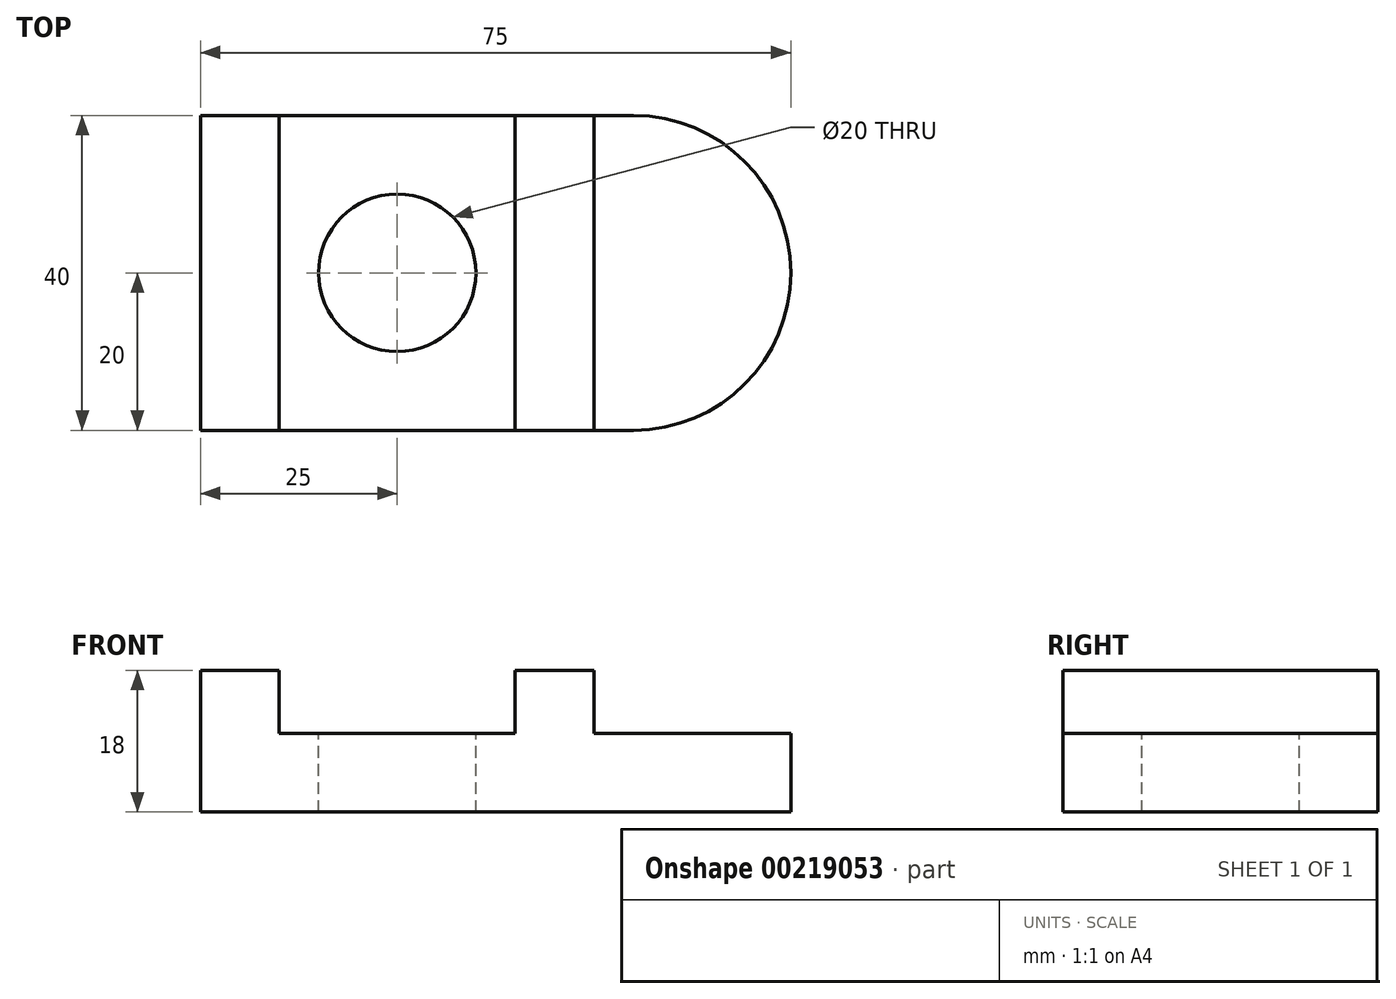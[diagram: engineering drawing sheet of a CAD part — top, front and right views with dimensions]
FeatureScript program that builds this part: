
annotation { "Feature Type Name" : "Feature", "Feature Type Description" : "" }
export const myFeature = defineFeature(function(context is Context, id is Id, definition is map)
    precondition{}
    {
        {
            var Q0;
            Q0=qCreatedBy(makeId("Front.planeOp"),FACE);
            var sketch = newSketch(context, id + "F0", { "sketchPlane" : qUnion([Q0])});
            skLineSegment(sketch, "E0", {"start": v(0, 0) * mm, "end": v(75, 0) * mm});
            skLineSegment(sketch, "E1", {"start": v(75, 0) * mm, "end": v(75, 10) * mm});
            skLineSegment(sketch, "E2", {"start": v(75, 10) * mm, "end": v(50, 10) * mm});
            skLineSegment(sketch, "E3", {"start": v(50, 10) * mm, "end": v(50, 18) * mm});
            skLineSegment(sketch, "E4", {"start": v(50, 18) * mm, "end": v(40, 18) * mm});
            skLineSegment(sketch, "E5", {"start": v(40, 18) * mm, "end": v(40, 10) * mm});
            skLineSegment(sketch, "E6", {"start": v(40, 10) * mm, "end": v(10, 10) * mm});
            skLineSegment(sketch, "E7", {"start": v(10, 10) * mm, "end": v(10, 18) * mm});
            skLineSegment(sketch, "E8", {"start": v(10, 18) * mm, "end": v(0, 18) * mm});
            skLineSegment(sketch, "E9", {"start": v(0, 18) * mm, "end": v(0, 0) * mm});
            skSolve(sketch);
        }
        {
            var Q0;
            Q0 = qSketchRegion(id + "F0", true);
            extrude(context, id + "F1", {"entities" : qUnion([Q0]), "depth" : 40 * mm});
        }
        {
            var Q0;
            Q0=makeQuery(id+"F1.opExtrude","CAP_EDGE",EDGE,{"disambiguationData":[OSD([sQuery(id+"F0.wireOp",EDGE,"E1")])],"isStart":false});
            var Q1;
            Q1=makeQuery(id+"F1.opExtrude","CAP_EDGE",EDGE,{"disambiguationData":[OSD([sQuery(id+"F0.wireOp",EDGE,"E1")])],"isStart":true});
            fillet(context, id + "F2", {"entities" : qUnion([Q0, Q1]), "radius" : 20 * mm, "tangentPropagation" : true, "allowEdgeOverflow" : false});
        }
        {
            var Q0;
            Q0=makeQuery(id+"F1.opExtrude","SWEPT_FACE",FACE,{"disambiguationData":[OSD([sQuery(id+"F0.wireOp",EDGE,"E6")])]});
            var sketch = newSketch(context, id + "F3", { "sketchPlane" : qUnion([Q0])});
            skCircle(sketch, "E10", {"center": v(25, -20) * mm, "radius": 10 * mm});
            skPoint(sketch, "E10.centerSnap0", {"position": v(40, -20) * mm});
            skPoint(sketch, "E10.centerSnap1", {"position": v(25, 0) * mm});
            skSolve(sketch);
        }
        {
            var Q0;
            Q0=makeQuery(id+"F3.imprint","IMPRINT",FACE,{"disambiguationData":[TD([[makeQuery(id+"F3.imprint","IMPRINT",EDGE,{"derivedFrom":sQuery(id+"F3.wireOp",EDGE,"E10")}),1.0]])]});
            extrude(context, id + "F4", {"entities" : qUnion([Q0]), "operationType" : NewBodyOperationType.REMOVE, "endBound" : BoundingType.UP_TO_NEXT, "oppositeDirection" : true, "depth" : 25 * mm});
        }
    });
